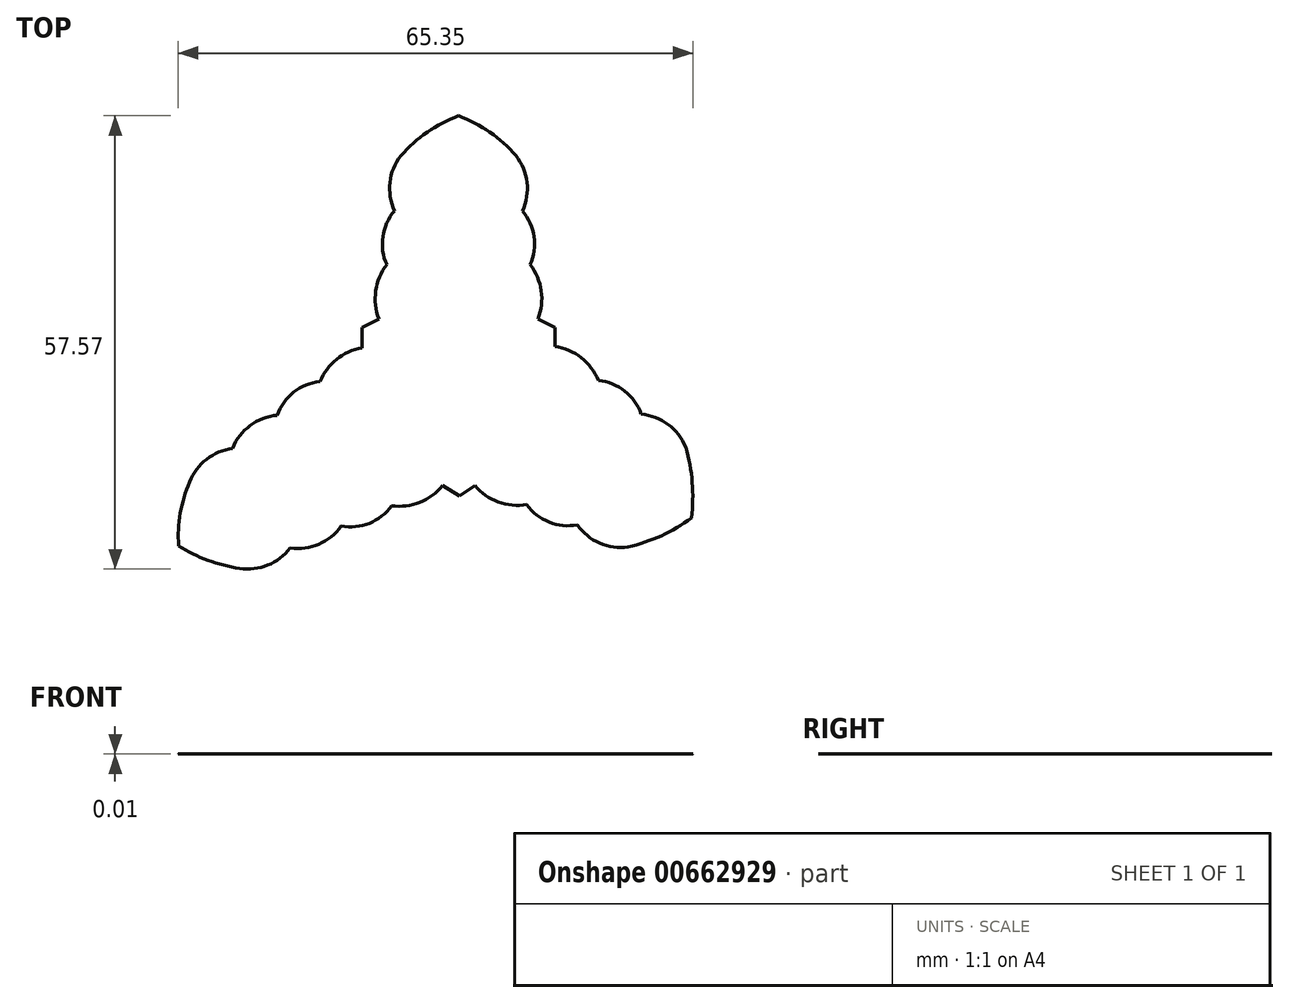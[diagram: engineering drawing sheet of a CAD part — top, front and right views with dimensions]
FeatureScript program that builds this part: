
annotation { "Feature Type Name" : "Feature", "Feature Type Description" : "" }
export const myFeature = defineFeature(function(context is Context, id is Id, definition is map)
    precondition{}
    {
        {
            var Q0;
            Q0=qCreatedBy(makeId("Top.planeOp"),FACE);
            var sketch = newSketch(context, id + "F0", { "sketchPlane" : qUnion([Q0])});
            skPoint(sketch, "E0.center", {"position": v(0, 0) * mm});
            skArc(sketch, "E1", {"start": v(-7.42, 28.98) * mm, "mid": v(-8.81, 25.6) * mm, "end": v(-8.23, 21.98) * mm});
            skArc(sketch, "E2", {"start": v(-8.23, 21.98) * mm, "mid": v(-9.72, 18.7) * mm, "end": v(-9.2, 15.13) * mm});
            skArc(sketch, "E3", {"start": v(-9.2, 15.13) * mm, "mid": v(-10.62, 11.82) * mm, "end": v(-10.2, 8.25) * mm});
            skLineSegment(sketch, "E4", {"start": v(-10.2, 8.25) * mm, "end": v(-12.37, 7.15) * mm});
            skLineSegment(sketch, "E5", {"start": v(-12.37, 7.15) * mm, "end": v(-12.37, 4.64) * mm});
            skLineSegment(sketch, "E6.MirrorCS", {"start": v(12.16, 7.15) * mm, "end": v(12.16, 4.64) * mm});
            skLineSegment(sketch, "E7.MirrorCS", {"start": v(10, 8.25) * mm, "end": v(12.16, 7.15) * mm});
            skArc(sketch, "E8.MirrorCS", {"start": v(9, 15.13) * mm, "mid": v(10.4, 11.82) * mm, "end": v(10, 8.25) * mm});
            skArc(sketch, "E9.MirrorCS", {"start": v(8.01, 21.98) * mm, "mid": v(9.5, 18.7) * mm, "end": v(9, 15.13) * mm});
            skArc(sketch, "E10.MirrorCS", {"start": v(7.2, 28.98) * mm, "mid": v(8.6, 25.6) * mm, "end": v(8.01, 21.98) * mm});
            skArc(sketch, "E11", {"start": v(28.76, -8.05) * mm, "mid": v(26.53, -5.15) * mm, "end": v(23.1, -3.85) * mm});
            skArc(sketch, "E12", {"start": v(23.1, -3.85) * mm, "mid": v(21, -0.92) * mm, "end": v(17.66, 0.43) * mm});
            skArc(sketch, "E13", {"start": v(17.66, 0.43) * mm, "mid": v(15.48, 3.32) * mm, "end": v(12.16, 4.74) * mm});
            skArc(sketch, "E14.MirrorCS", {"start": v(8.56, -15.34) * mm, "mid": v(4.94, -15) * mm, "end": v(1.97, -12.9) * mm});
            skArc(sketch, "E15.MirrorCS", {"start": v(14.98, -17.91) * mm, "mid": v(11.4, -17.56) * mm, "end": v(8.56, -15.34) * mm});
            skArc(sketch, "E16.MirrorCS", {"start": v(21.45, -20.71) * mm, "mid": v(17.82, -20.23) * mm, "end": v(14.98, -17.91) * mm});
            skLineSegment(sketch, "E17", {"start": v(1.97, -12.9) * mm, "end": v(0, -14.26) * mm});
            skLineSegment(sketch, "E18", {"start": v(0, -14.26) * mm, "end": v(-2.14, -12.9) * mm});
            skArc(sketch, "E19", {"start": v(-27.91, -23.45) * mm, "mid": v(-24.35, -23.03) * mm, "end": v(-21.5, -20.86) * mm});
            skArc(sketch, "E20", {"start": v(-21.5, -20.86) * mm, "mid": v(-17.86, -20.37) * mm, "end": v(-15.02, -18.05) * mm});
            skArc(sketch, "E21", {"start": v(-15.02, -18.05) * mm, "mid": v(-11.43, -17.7) * mm, "end": v(-8.6, -15.48) * mm});
            skArc(sketch, "E22", {"start": v(-8.6, -15.48) * mm, "mid": v(-5.03, -15.05) * mm, "end": v(-2.14, -12.9) * mm});
            skArc(sketch, "E23.MirrorCS", {"start": v(-17.7, 0.28) * mm, "mid": v(-15.6, 3.12) * mm, "end": v(-12.37, 4.57) * mm});
            skArc(sketch, "E24.MirrorCS", {"start": v(-23.14, -4) * mm, "mid": v(-21.05, -1.06) * mm, "end": v(-17.7, 0.28) * mm});
            skArc(sketch, "E25.MirrorCS", {"start": v(-28.8, -8.2) * mm, "mid": v(-26.56, -5.3) * mm, "end": v(-23.14, -4) * mm});
            skArc(sketch, "E26.MirrorCS", {"start": v(-34.25, -12.46) * mm, "mid": v(-32.11, -9.58) * mm, "end": v(-28.8, -8.2) * mm});
            skLineSegment(sketch, "E27", {"start": v(-12.37, 4.64) * mm, "end": v(-12.37, 4.57) * mm});
            skArc(sketch, "E28", {"start": v(-34.25, -12.46) * mm, "mid": v(-35.45, -16.43) * mm, "end": v(-35.66, -20.56) * mm});
            skArc(sketch, "E29", {"start": v(-35.66, -20.56) * mm, "mid": v(-31.94, -22.42) * mm, "end": v(-27.91, -23.45) * mm});
            skArc(sketch, "E30", {"start": v(-0.1, 34.05) * mm, "mid": v(-4.07, 31.97) * mm, "end": v(-7.42, 28.98) * mm});
            skArc(sketch, "E31", {"start": v(7.2, 28.98) * mm, "mid": v(3.87, 31.97) * mm, "end": v(-0.1, 34.05) * mm});
            skArc(sketch, "E32", {"start": v(21.45, -20.71) * mm, "mid": v(25.66, -19.3) * mm, "end": v(29.48, -17.04) * mm});
            skArc(sketch, "E33", {"start": v(29.48, -17.04) * mm, "mid": v(29.58, -12.51) * mm, "end": v(28.76, -8.05) * mm});
            skSolve(sketch);
        }
        {
            var Q0;
            Q0=makeQuery(id+"F0.imprint","IMPRINT",FACE,{"disambiguationData":[TD([[makeQuery(id+"F0.imprint","IMPRINT",EDGE,{"derivedFrom":sQuery(id+"F0.wireOp",EDGE,"E1")}),1.0]])]});
            extrude(context, id + "F1", {"entities" : qUnion([Q0]), "depth" : 5 / 406.4 * mm, "offsetDistance" : 25.4 * mm});
        }
    });
